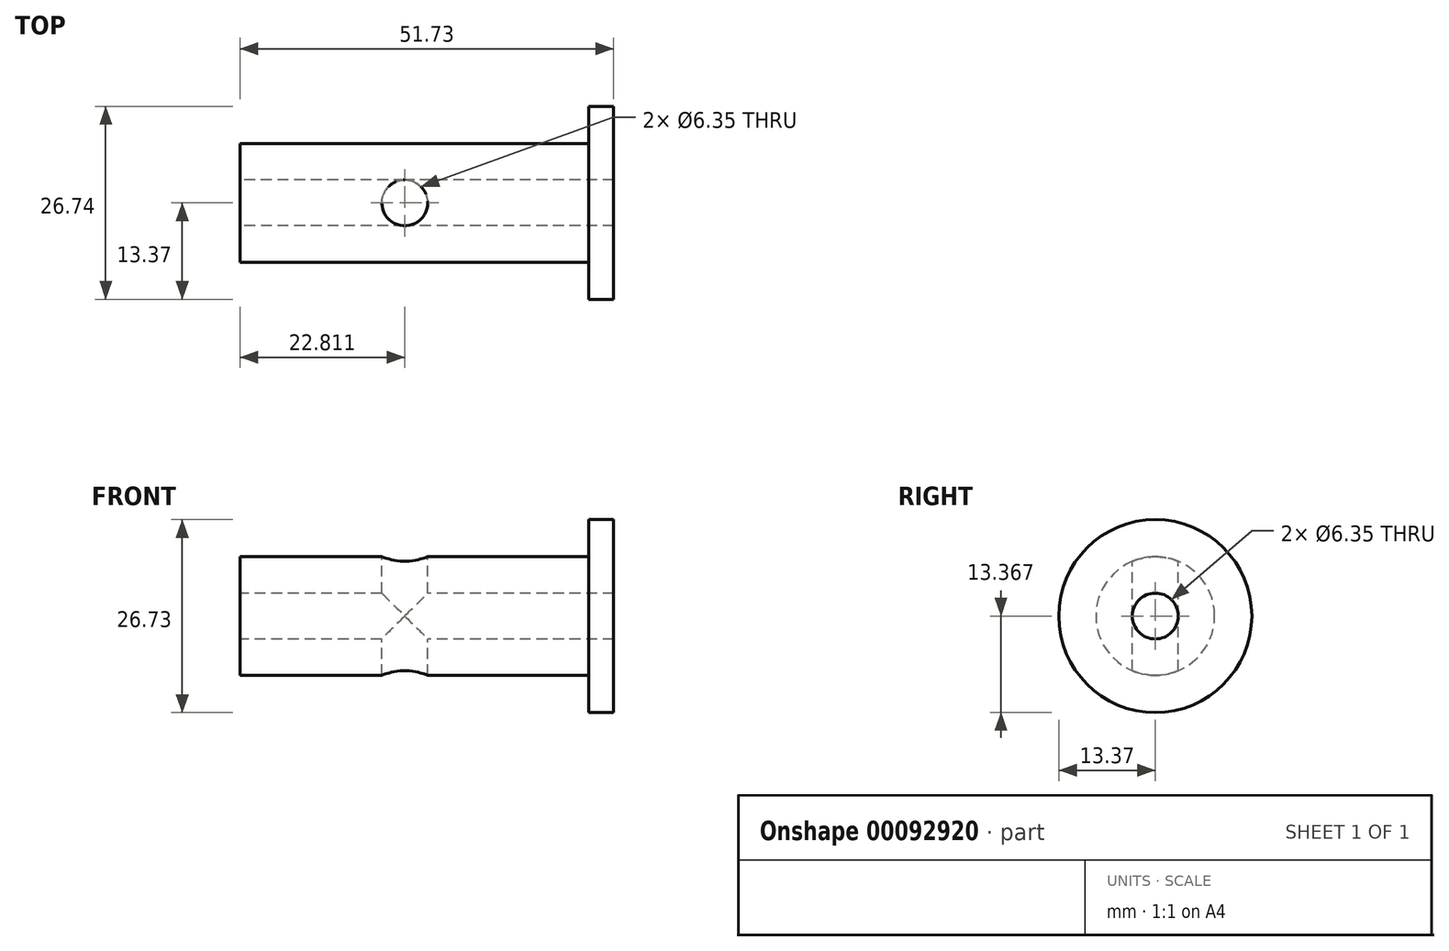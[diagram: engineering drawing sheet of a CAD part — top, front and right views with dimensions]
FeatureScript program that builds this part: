
annotation { "Feature Type Name" : "Feature", "Feature Type Description" : "" }
export const myFeature = defineFeature(function(context is Context, id is Id, definition is map)
    precondition{}
    {
        {
            var Q0;
            Q0=qCreatedBy(makeId("Front.planeOp"),FACE);
            var sketch = newSketch(context, id + "F0", { "sketchPlane" : qUnion([Q0])});
            skLineSegment(sketch, "E0", {"start": v(387.68, 44.25) * mm, "end": v(387.68, 54.44) * mm});
            skLineSegment(sketch, "E1", {"start": v(387.68, 54.44) * mm, "end": v(384.2, 54.44) * mm});
            skLineSegment(sketch, "E2", {"start": v(384.2, 54.44) * mm, "end": v(384.2, 49.3) * mm});
            skLineSegment(sketch, "E3", {"start": v(384.2, 49.3) * mm, "end": v(361.43, 49.3) * mm});
            skLineSegment(sketch, "E4", {"start": v(335.95, 49.3) * mm, "end": v(335.95, 44.25) * mm});
            skLineSegment(sketch, "E5", {"start": v(335.95, 44.25) * mm, "end": v(387.68, 44.25) * mm});
            skLineSegment(sketch, "E6", {"start": v(325.63, 41.08) * mm, "end": v(408.78, 41.08) * mm, "construction": true});
            skLineSegment(sketch, "E7", {"start": v(356.09, 49.3) * mm, "end": v(356.09, 44.25) * mm, "construction": true});
            skLineSegment(sketch, "E8", {"start": v(361.43, 49.3) * mm, "end": v(361.43, 44.25) * mm, "construction": true});
            skLineSegment(sketch, "E9", {"start": v(358.76, 49.3) * mm, "end": v(356.09, 49.3) * mm});
            skLineSegment(sketch, "E10", {"start": v(356.09, 49.3) * mm, "end": v(335.95, 49.3) * mm});
            skLineSegment(sketch, "E11", {"start": v(361.43, 49.3) * mm, "end": v(358.76, 49.3) * mm});
            skSolve(sketch);
        }
        {
            var Q0;
            Q0=makeQuery(id+"F0.imprint","IMPRINT",FACE,{"disambiguationData":[TD([[makeQuery(id+"F0.imprint","IMPRINT",EDGE,{"derivedFrom":sQuery(id+"F0.wireOp",EDGE,"E0")}),1.0]])]});
            var Q1;
            Q1=sQuery(id+"F0.wireOp",EDGE,"E6");
            revolve(context, id + "F1", {"entities" : qUnion([Q0]), "axis" : qUnion([Q1]), "revolveType" : RevolveType.FULL});
        }
        {
            var Q0;
            Q0=qCreatedBy(makeId("Top.planeOp"),FACE);
            var Q1;
            Q1=sQuery(id+"F0.wireOp",VERTEX,"E11.end");
            cPlane(context, id + "F2", {"entities" : qUnion([Q0, Q1]), "cplaneType" : CPlaneType.PLANE_POINT, "offset" : 152.4 * mm, "width" : 152.4 * mm, "height" : 152.4 * mm});
        }
        {
            var Q0;
            Q0=qCreatedBy(id+"F2.planeOp",FACE);
            var sketch = newSketch(context, id + "F3", { "sketchPlane" : qUnion([Q0])});
            skPoint(sketch, "E12", {"position": v(358.76, 0) * mm});
            skSolve(sketch);
        }
        {
            var Q0;
            Q0=sQuery(id+"F3.wireOp",VERTEX,"E12");
            var Q1;
            Q1=makeQuery(id+"F1.opRevolve","SWEPT_BODY",BODY,{"disambiguationData":[OSD([sQuery(id+"F0.wireOp",EDGE,"E0"),sQuery(id+"F0.wireOp",EDGE,"E1"),sQuery(id+"F0.wireOp",EDGE,"E2"),sQuery(id+"F0.wireOp",EDGE,"E3"),sQuery(id+"F0.wireOp",EDGE,"E4"),sQuery(id+"F0.wireOp",EDGE,"E5"),sQuery(id+"F0.wireOp",EDGE,"E9"),sQuery(id+"F0.wireOp",EDGE,"E10"),sQuery(id+"F0.wireOp",EDGE,"E11")])]});
            hole(context, id + "F4", {"style" : HoleStyle.SIMPLE, "holeDiameter" : 6.35 * mm, "endStyle" : HoleEndStyle.THROUGH, "locations" : qUnion([Q0]), "scope" : qUnion([Q1])});
        }
    });
